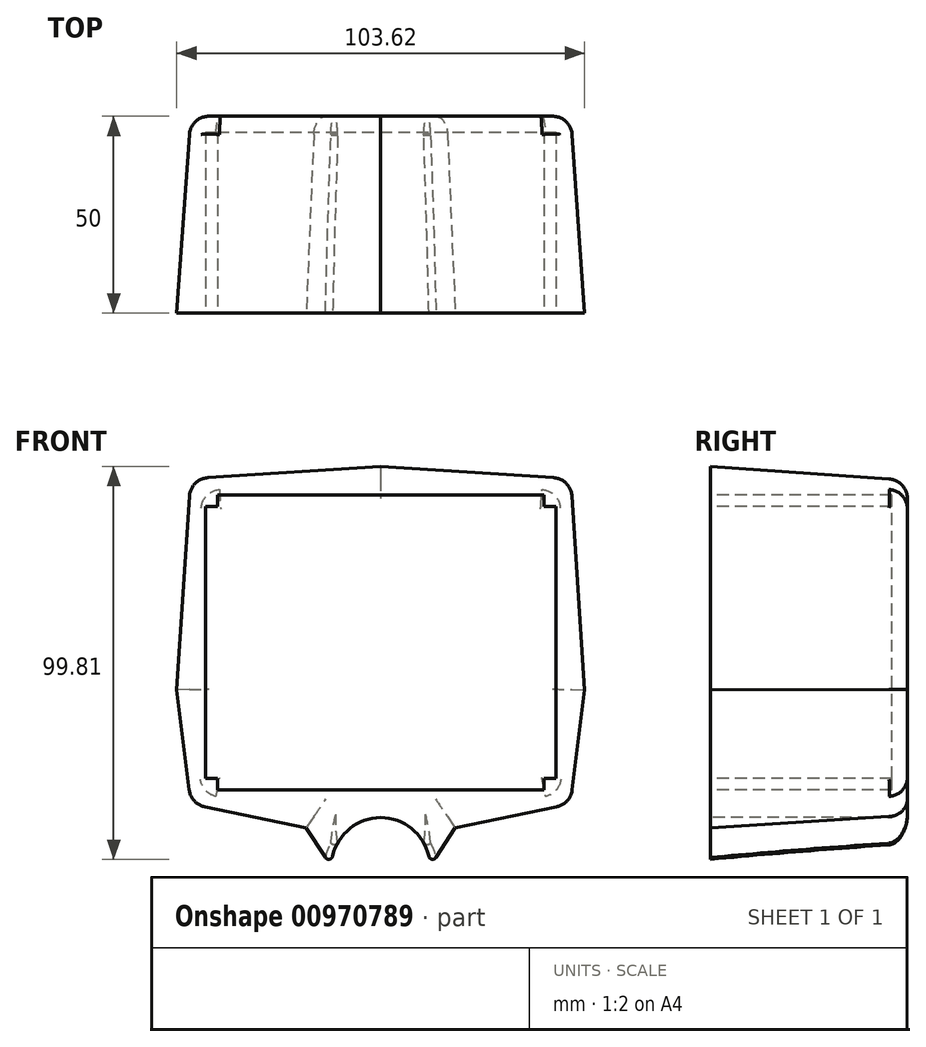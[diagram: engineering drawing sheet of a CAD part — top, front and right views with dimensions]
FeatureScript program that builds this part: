
annotation { "Feature Type Name" : "Feature", "Feature Type Description" : "" }
export const myFeature = defineFeature(function(context is Context, id is Id, definition is map)
    precondition{}
    {
        {
            var Q0;
            Q0=qCreatedBy(makeId("Front.planeOp"),FACE);
            var sketch = newSketch(context, id + "F0", { "sketchPlane" : qUnion([Q0])});
            skLineSegment(sketch, "E0.bottom", {"start": v(-44.5, 39.5) * mm, "end": v(44.5, 39.5) * mm});
            skLineSegment(sketch, "E0.top", {"start": v(-44.5, -39.5) * mm, "end": v(44.5, -39.5) * mm});
            skLineSegment(sketch, "E0.left", {"start": v(-46.5, 37.5) * mm, "end": v(-46.5, -37.5) * mm});
            skLineSegment(sketch, "E0.right", {"start": v(46.5, 37.5) * mm, "end": v(46.5, -37.5) * mm});
            skPoint(sketch, "E1.middle", {"position": v(0, 0) * mm});
            skPoint(sketch, "E1.middle.positionSnap0", {"position": v(-46.5, 0) * mm});
            skPoint(sketch, "E1.middle.positionSnap1", {"position": v(0, 39.5) * mm});
            skPoint(sketch, "E1.centerSnap0", {"position": v(-46.5, 0) * mm});
            skPoint(sketch, "E1.centerSnap1", {"position": v(0, 39.5) * mm});
            skLineSegment(sketch, "E2", {"start": v(0, 55.5) * mm, "end": v(0, -44.5) * mm, "construction": true});
            skLineSegment(sketch, "E3", {"start": v(-48.86, 0.37) * mm, "end": v(-48.86, 0.37) * mm});
            skArc(sketch, "E4", {"start": v(12.5, -57) * mm, "mid": v(0, -44.5) * mm, "end": v(-12.5, -57) * mm});
            skLineSegment(sketch, "E5", {"start": v(-12.5, -57) * mm, "end": v(12.5, -57) * mm});
            skPoint(sketch, "E6.visualSharp", {"position": v(46.5, 39.5) * mm});
            skArc(sketch, "E6.filletArc", {"start": v(46.5, 37.5) * mm, "mid": v(45.91, 38.91) * mm, "end": v(44.5, 39.5) * mm});
            skPoint(sketch, "E7.visualSharp", {"position": v(-46.5, 39.5) * mm});
            skArc(sketch, "E7.filletArc", {"start": v(-44.5, 39.5) * mm, "mid": v(-45.91, 38.91) * mm, "end": v(-46.5, 37.5) * mm});
            skPoint(sketch, "E8.visualSharp", {"position": v(46.5, -39.5) * mm});
            skArc(sketch, "E8.filletArc", {"start": v(44.5, -39.5) * mm, "mid": v(45.91, -38.91) * mm, "end": v(46.5, -37.5) * mm});
            skPoint(sketch, "E9.visualSharp", {"position": v(-46.5, -39.5) * mm});
            skArc(sketch, "E9.filletArc", {"start": v(-46.5, -37.5) * mm, "mid": v(-45.91, -38.91) * mm, "end": v(-44.5, -39.5) * mm});
            skLineSegment(sketch, "E10", {"start": v(-12.5, -57) * mm, "end": v(-18.93, -47.08) * mm});
            skLineSegment(sketch, "E11", {"start": v(-18.93, -47.08) * mm, "end": v(-48.2, -41.04) * mm});
            skLineSegment(sketch, "E12", {"start": v(-48.2, -41.04) * mm, "end": v(-51.81, -12.07) * mm});
            skLineSegment(sketch, "E13", {"start": v(-51.81, -12.07) * mm, "end": v(-48.3, 41.58) * mm});
            skLineSegment(sketch, "E14", {"start": v(-48.3, 41.58) * mm, "end": v(0, 44.7) * mm});
            skLineSegment(sketch, "E15.MirrorCS", {"start": v(48.3, 41.58) * mm, "end": v(0, 44.7) * mm});
            skLineSegment(sketch, "E16.MirrorCS", {"start": v(51.81, -12.07) * mm, "end": v(48.3, 41.58) * mm});
            skLineSegment(sketch, "E17.MirrorCS", {"start": v(48.2, -41.04) * mm, "end": v(51.81, -12.07) * mm});
            skLineSegment(sketch, "E18.MirrorCS", {"start": v(18.93, -47.08) * mm, "end": v(48.2, -41.04) * mm});
            skLineSegment(sketch, "E19.MirrorCS", {"start": v(12.5, -57) * mm, "end": v(18.93, -47.08) * mm});
            skLineSegment(sketch, "E20.left", {"start": v(44.5, -34.5) * mm, "end": v(44.5, 34.5) * mm, "construction": true});
            skLineSegment(sketch, "E20.right", {"start": v(-44.5, -34.5) * mm, "end": v(-44.5, 34.5) * mm, "construction": true});
            skLineSegment(sketch, "E21.top", {"start": v(41.5, 37.5) * mm, "end": v(-41.5, 37.5) * mm, "construction": true});
            skLineSegment(sketch, "E22", {"start": v(-44.5, 34.5) * mm, "end": v(-41.5, 34.5) * mm});
            skLineSegment(sketch, "E23", {"start": v(-41.5, 37.5) * mm, "end": v(41.5, 37.5) * mm});
            skLineSegment(sketch, "E24", {"start": v(41.5, 34.5) * mm, "end": v(44.5, 34.5) * mm});
            skLineSegment(sketch, "E25", {"start": v(44.5, 34.5) * mm, "end": v(44.5, -34.5) * mm});
            skLineSegment(sketch, "E26", {"start": v(41.5, -34.5) * mm, "end": v(41.5, -37.5) * mm});
            skLineSegment(sketch, "E27", {"start": v(-41.5, -37.5) * mm, "end": v(-41.5, -34.5) * mm});
            skLineSegment(sketch, "E28", {"start": v(-44.5, -34.5) * mm, "end": v(-44.5, 34.5) * mm});
            skLineSegment(sketch, "E29", {"start": v(41.5, 34.5) * mm, "end": v(41.5, 37.5) * mm});
            skLineSegment(sketch, "E30", {"start": v(-41.5, 34.5) * mm, "end": v(-41.5, 37.5) * mm});
            skLineSegment(sketch, "E31", {"start": v(-44.5, -34.5) * mm, "end": v(-41.5, -34.5) * mm});
            skLineSegment(sketch, "E32", {"start": v(41.5, -34.5) * mm, "end": v(44.5, -34.5) * mm});
            skLineSegment(sketch, "E33", {"start": v(-41.5, -37.5) * mm, "end": v(41.5, -37.5) * mm});
            skSolve(sketch);
        }
        {
            var Q0;
            Q0=makeQuery(id+"F0.imprint","IMPRINT",FACE,{"disambiguationData":[TD([[makeQuery(id+"F0.imprint","IMPRINT",EDGE,{"derivedFrom":sQuery(id+"F0.wireOp",EDGE,"E22")}),-1.0]])]});
            var Q1;
            Q1=makeQuery(id+"F0.imprint","IMPRINT",FACE,{"disambiguationData":[TD([[makeQuery(id+"F0.imprint","IMPRINT",EDGE,{"derivedFrom":sQuery(id+"F0.wireOp",EDGE,"E0.bottom")}),-1.0]])]});
            var Q2;
            Q2=makeQuery(id+"F0.imprint","IMPRINT",FACE,{"disambiguationData":[TD([[makeQuery(id+"F0.imprint","IMPRINT",EDGE,{"derivedFrom":sQuery(id+"F0.wireOp",EDGE,"E4")}),1.0]])]});
            var Q3;
            Q3=makeQuery(id+"F0.imprint","IMPRINT",FACE,{"disambiguationData":[TD([[makeQuery(id+"F0.imprint","IMPRINT",EDGE,{"derivedFrom":sQuery(id+"F0.wireOp",EDGE,"E0.bottom")}),1.0]])]});
            extrude(context, id + "F1", {"entities" : qUnion([Q0, Q1, Q2, Q3]), "oppositeDirection" : true, "depth" : 50 * mm, "offsetDistance" : 25 * mm, "hasDraft" : true, "draftAngle" : 4 * degree, "draftPullDirection" : true});
        }
        {
            var Q0;
            Q0=makeQuery(id+"F0.imprint","IMPRINT",FACE,{"disambiguationData":[TD([[makeQuery(id+"F0.imprint","IMPRINT",EDGE,{"derivedFrom":sQuery(id+"F0.wireOp",EDGE,"E4")}),1.0]])]});
            extrude(context, id + "F2", {"entities" : qUnion([Q0]), "operationType" : NewBodyOperationType.REMOVE, "oppositeDirection" : true, "depth" : 50 * mm, "offsetDistance" : 25 * mm});
        }
        {
            var Q0;
            Q0=makeQuery(id+"F0.imprint","IMPRINT",FACE,{"disambiguationData":[TD([[makeQuery(id+"F0.imprint","IMPRINT",EDGE,{"derivedFrom":sQuery(id+"F0.wireOp",EDGE,"E22")}),-1.0]])]});
            extrude(context, id + "F3", {"entities" : qUnion([Q0]), "operationType" : NewBodyOperationType.REMOVE, "oppositeDirection" : true, "depth" : 46 * mm, "offsetDistance" : 25 * mm});
        }
        {
            var Q0;
            Q0=makeQuery(id+"F1.opExtrude","CAP_FACE",FACE,{"disambiguationData":[OSD([sQuery(id+"F0.wireOp",EDGE,"E5"),sQuery(id+"F0.wireOp",EDGE,"E10"),sQuery(id+"F0.wireOp",EDGE,"E11"),sQuery(id+"F0.wireOp",EDGE,"E12"),sQuery(id+"F0.wireOp",EDGE,"E13"),sQuery(id+"F0.wireOp",EDGE,"E14"),sQuery(id+"F0.wireOp",EDGE,"E15.MirrorCS"),sQuery(id+"F0.wireOp",EDGE,"E16.MirrorCS"),sQuery(id+"F0.wireOp",EDGE,"E17.MirrorCS"),sQuery(id+"F0.wireOp",EDGE,"E18.MirrorCS"),sQuery(id+"F0.wireOp",EDGE,"E19.MirrorCS")])],"isStart":false});
            fillet(context, id + "F4", {"entities" : qUnion([Q0]), "radius" : 5 * mm, "tangentPropagation" : true, "allowEdgeOverflow" : false});
        }
        {
            var Q0;
            Q0=makeQuery(id+"F2.boolean.opBoolean","INTERSECT",EDGE,{"derivedFrom":[makeQuery(id+"F1.opExtrude","SWEPT_FACE",FACE,{"disambiguationData":[OSD([sQuery(id+"F0.wireOp",EDGE,"E19.MirrorCS")])]}),makeQuery(id+"F2.opExtrude","SWEPT_FACE",FACE,{"disambiguationData":[OSD([sQuery(id+"F0.wireOp",EDGE,"E4")])]})]});
            var Q1;
            Q1=makeQuery(id+"F2.boolean.opBoolean","INTERSECT",EDGE,{"derivedFrom":[makeQuery(id+"F1.opExtrude","SWEPT_FACE",FACE,{"disambiguationData":[OSD([sQuery(id+"F0.wireOp",EDGE,"E10")])]}),makeQuery(id+"F2.opExtrude","SWEPT_FACE",FACE,{"disambiguationData":[OSD([sQuery(id+"F0.wireOp",EDGE,"E4")])]})]});
            fillet(context, id + "F5", {"entities" : qUnion([Q0, Q1]), "radius" : 1 * mm, "tangentPropagation" : true, "allowEdgeOverflow" : false});
        }
        {
            var Q0;
            Q0=makeQuery(id+"F1.opExtrude","SWEPT_EDGE",EDGE,{"disambiguationData":[OSD([sQuery(id+"F0.wireOp",EDGE,"E17.MirrorCS"),sQuery(id+"F0.wireOp",EDGE,"E18.MirrorCS")])]});
            var Q1;
            Q1=makeQuery(id+"F1.opExtrude","SWEPT_EDGE",EDGE,{"disambiguationData":[OSD([sQuery(id+"F0.wireOp",EDGE,"E11"),sQuery(id+"F0.wireOp",EDGE,"E12")])]});
            var Q2;
            Q2=makeQuery(id+"F1.opExtrude","SWEPT_EDGE",EDGE,{"disambiguationData":[OSD([sQuery(id+"F0.wireOp",EDGE,"E13"),sQuery(id+"F0.wireOp",EDGE,"E14")])]});
            var Q3;
            Q3=makeQuery(id+"F1.opExtrude","SWEPT_EDGE",EDGE,{"disambiguationData":[OSD([sQuery(id+"F0.wireOp",EDGE,"E15.MirrorCS"),sQuery(id+"F0.wireOp",EDGE,"E16.MirrorCS")])]});
            fillet(context, id + "F6", {"entities" : qUnion([Q0, Q1, Q2, Q3]), "radius" : 5 * mm, "tangentPropagation" : true, "allowEdgeOverflow" : false});
        }
    });
